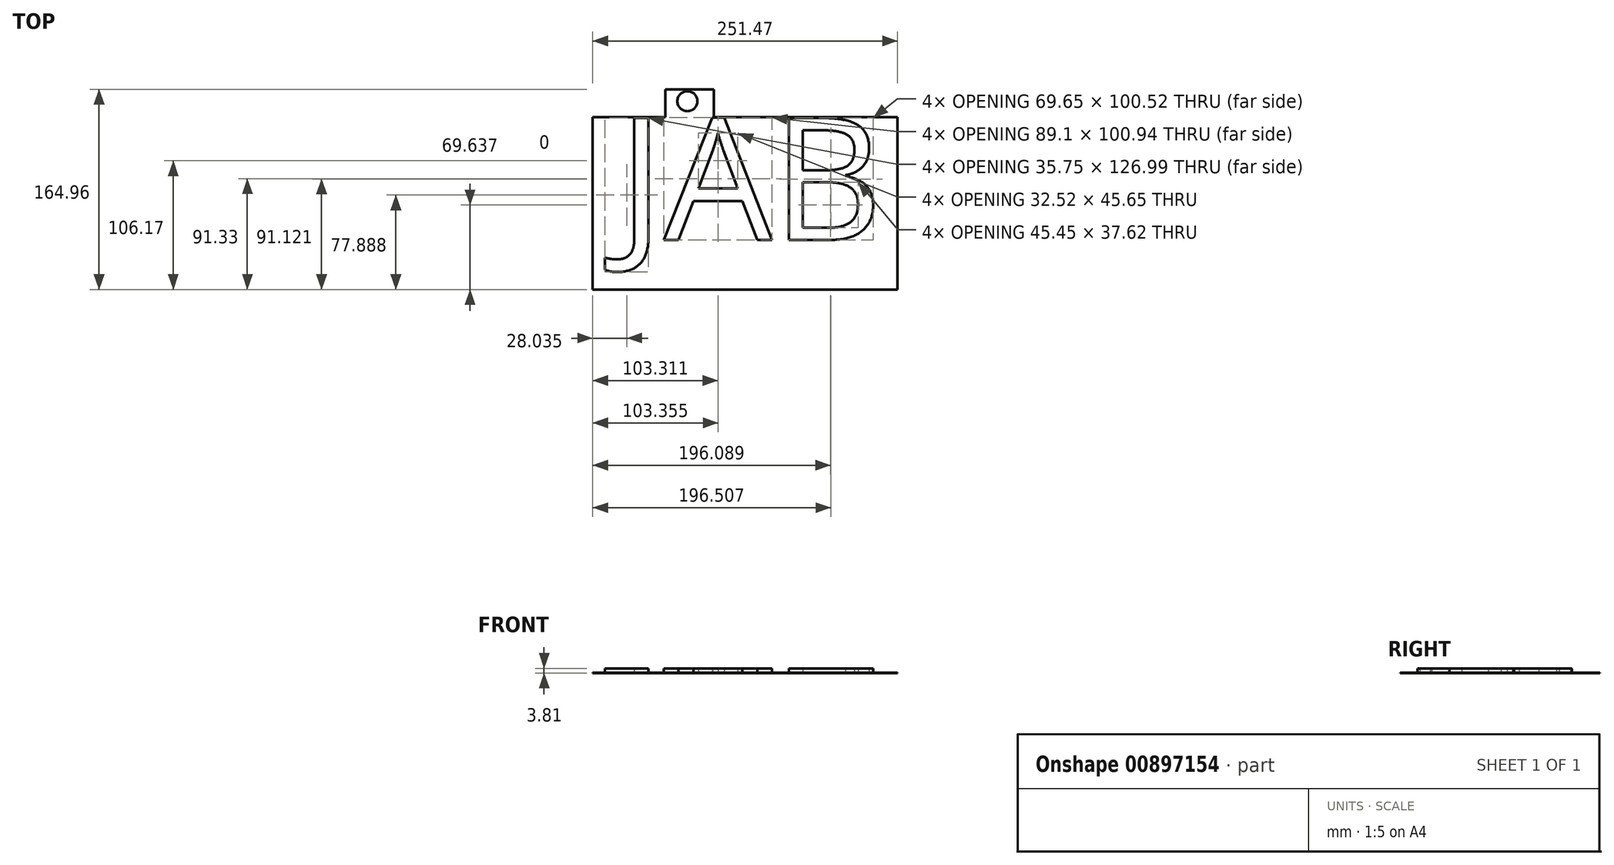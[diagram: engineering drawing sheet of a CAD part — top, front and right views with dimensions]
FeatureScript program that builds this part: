
annotation { "Feature Type Name" : "Feature", "Feature Type Description" : "" }
export const myFeature = defineFeature(function(context is Context, id is Id, definition is map)
    precondition{}
    {
        {
            var Q0;
            Q0=qCreatedBy(makeId("Top.planeOp"),FACE);
            var sketch = newSketch(context, id + "F0", { "sketchPlane" : qUnion([Q0])});
            skText(sketch, "E0", { "text": "JAB", "fontName": "OpenSans-Regular.ttf"});
            skLineSegment(sketch, "E1", {"start": v(-54.01, 55.52) * mm, "end": v(176.3, 55.52) * mm});
            skLineSegment(sketch, "E2", {"start": v(176.3, 55.52) * mm, "end": v(176.3, -86.72) * mm});
            skLineSegment(sketch, "E3", {"start": v(176.3, -86.72) * mm, "end": v(-75.17, -86.72) * mm});
            skLineSegment(sketch, "E4", {"start": v(-75.17, -86.72) * mm, "end": v(-75.17, 55.52) * mm});
            skLineSegment(sketch, "E5", {"start": v(-75.17, 55.52) * mm, "end": v(-54.01, 55.52) * mm});
            skLineSegment(sketch, "E6", {"start": v(-15.27, 78.24) * mm, "end": v(-15.27, 55.52) * mm});
            skLineSegment(sketch, "E7", {"start": v(-15.27, 78.24) * mm, "end": v(24.83, 78.24) * mm});
            skLineSegment(sketch, "E8", {"start": v(24.83, 78.24) * mm, "end": v(24.83, 55.52) * mm});
            skCircle(sketch, "E9", {"center": v(2.9, 68.52) * mm, "radius": 4.78 * mm});
            skCircle(sketch, "E10", {"center": v(2.9, 68.52) * mm, "radius": 8.27 * mm});
            const initialGuessF0  = {"E0": [-0.05401, -0.04586, 1, 0, 0.10138]};
            skSetInitialGuess(sketch, initialGuessF0);
            skSolve(sketch);
        }
        {
            var Q0;
            Q0=makeQuery(id+"F0.imprint","IMPRINT",FACE,{"disambiguationData":[TD([[makeQuery(id+"F0.imprint","IMPRINT",EDGE,{"derivedFrom":sQuery(id+"F0.wireOp",EDGE,"E0.sketch_text.stroke-0")}),-1.0]])]});
            var Q1;
            Q1=makeQuery(id+"F0.imprint","IMPRINT",FACE,{"disambiguationData":[TD([[makeQuery(id+"F0.imprint","IMPRINT",EDGE,{"derivedFrom":sQuery(id+"F0.wireOp",EDGE,"E0.sketch_text.stroke-10")}),-1.0]])]});
            var Q2;
            Q2=makeQuery(id+"F0.imprint","IMPRINT",FACE,{"disambiguationData":[TD([[makeQuery(id+"F0.imprint","IMPRINT",EDGE,{"derivedFrom":sQuery(id+"F0.wireOp",EDGE,"E0.sketch_text.stroke-23")}),-1.0]])]});
            extrude(context, id + "F1", {"entities" : qUnion([Q0, Q1, Q2]), "depth" : 3.8 * mm, "offsetDistance" : 25.4 * mm});
        }
        {
            var Q0;
            Q0 = qSketchRegion(id + "F0", true);
            extrude(context, id + "F2", {"entities" : qUnion([Q0]), "depth" : 0.25 * mm, "offsetDistance" : 25.4 * mm});
        }
    });
